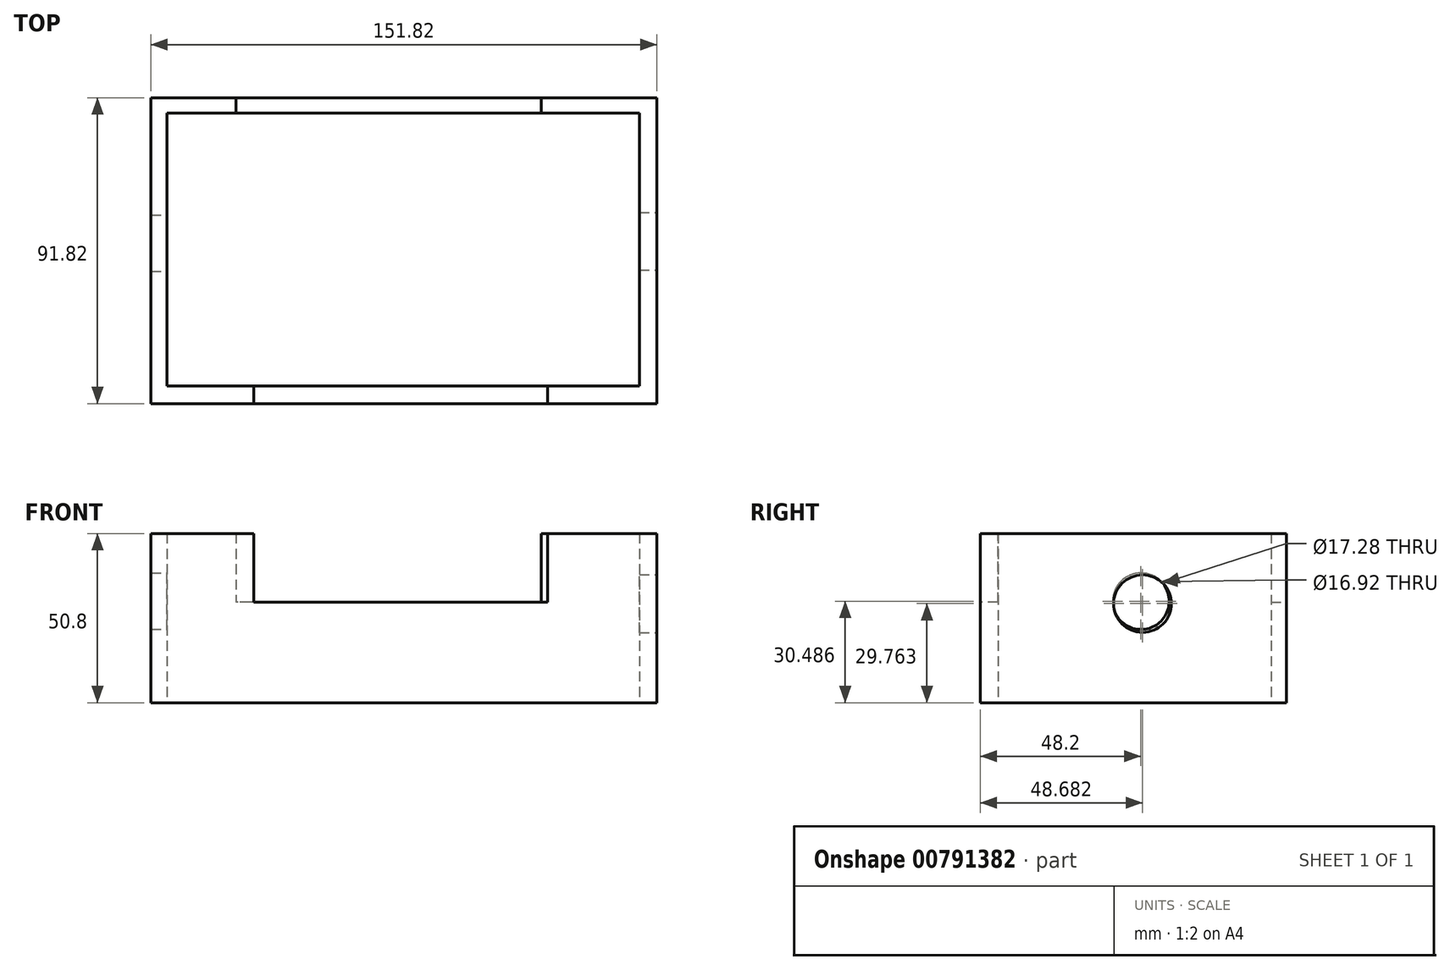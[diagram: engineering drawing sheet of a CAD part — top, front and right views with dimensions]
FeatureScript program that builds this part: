
annotation { "Feature Type Name" : "Feature", "Feature Type Description" : "" }
export const myFeature = defineFeature(function(context is Context, id is Id, definition is map)
    precondition{}
    {
        {
            var Q0;
            Q0=qCreatedBy(makeId("Top.planeOp"),FACE);
            var sketch = newSketch(context, id + "F0", { "sketchPlane" : qUnion([Q0])});
            skLineSegment(sketch, "E0.bottom", {"start": v(-76.03, 36.27) * mm, "end": v(75.8, 36.27) * mm});
            skLineSegment(sketch, "E0.top", {"start": v(-76.03, -55.55) * mm, "end": v(75.8, -55.55) * mm});
            skLineSegment(sketch, "E0.left", {"start": v(-76.03, 36.27) * mm, "end": v(-76.03, -55.55) * mm});
            skLineSegment(sketch, "E0.right", {"start": v(75.8, 36.27) * mm, "end": v(75.8, -55.55) * mm});
            skLineSegment(sketch, "E1.bottom", {"start": v(-71.21, 31.7) * mm, "end": v(70.5, 31.7) * mm});
            skLineSegment(sketch, "E1.top", {"start": v(-71.21, -50.25) * mm, "end": v(70.5, -50.25) * mm});
            skLineSegment(sketch, "E1.left", {"start": v(-71.21, 31.7) * mm, "end": v(-71.21, -50.25) * mm});
            skLineSegment(sketch, "E1.right", {"start": v(70.5, 31.7) * mm, "end": v(70.5, -50.25) * mm});
            skSolve(sketch);
        }
        {
            var Q0;
            Q0=makeQuery(id+"F0.imprint","IMPRINT",FACE,{"disambiguationData":[TD([[makeQuery(id+"F0.imprint","IMPRINT",EDGE,{"derivedFrom":sQuery(id+"F0.wireOp",EDGE,"E0.bottom")}),-1.0]])]});
            extrude(context, id + "F1", {"entities" : qUnion([Q0]), "depth" : 50.8 * mm, "offsetDistance" : 25.4 * mm});
        }
        {
            var Q0;
            Q0=makeQuery(id+"F1.opExtrude","SWEPT_FACE",FACE,{"disambiguationData":[OSD([sQuery(id+"F0.wireOp",EDGE,"E0.top")])]});
            var sketch = newSketch(context, id + "F2", { "sketchPlane" : qUnion([Q0])});
            skLineSegment(sketch, "E2.bottom", {"start": v(-45.2, 50.8) * mm, "end": v(42.95, 50.8) * mm});
            skLineSegment(sketch, "E2.top", {"start": v(-45.2, 30.18) * mm, "end": v(42.95, 30.18) * mm});
            skLineSegment(sketch, "E2.left", {"start": v(-45.2, 50.8) * mm, "end": v(-45.2, 30.18) * mm});
            skLineSegment(sketch, "E2.right", {"start": v(42.95, 50.8) * mm, "end": v(42.95, 30.18) * mm});
            skSolve(sketch);
        }
        {
            var Q0;
            Q0=makeQuery(id+"F2.imprint","IMPRINT",FACE,{"disambiguationData":[TD([[makeQuery(id+"F2.imprint","IMPRINT",EDGE,{"derivedFrom":sQuery(id+"F2.wireOp",EDGE,"E2.bottom")}),-1.0]])]});
            extrude(context, id + "F3", {"entities" : qUnion([Q0]), "operationType" : NewBodyOperationType.REMOVE, "oppositeDirection" : true, "depth" : 25.4 * mm, "offsetDistance" : 25.4 * mm});
        }
        {
            var Q0;
            Q0=makeQuery(id+"F1.opExtrude","SWEPT_FACE",FACE,{"disambiguationData":[OSD([sQuery(id+"F0.wireOp",EDGE,"E0.right")])]});
            var sketch = newSketch(context, id + "F4", { "sketchPlane" : qUnion([Q0])});
            skCircle(sketch, "E3", {"center": v(-6.87, 29.76) * mm, "radius": 8.64 * mm});
            skSolve(sketch);
        }
        {
            var Q0;
            Q0=makeQuery(id+"F4.imprint","IMPRINT",FACE,{"disambiguationData":[TD([[makeQuery(id+"F4.imprint","IMPRINT",EDGE,{"derivedFrom":sQuery(id+"F4.wireOp",EDGE,"E3")}),1.0]])]});
            extrude(context, id + "F5", {"entities" : qUnion([Q0]), "operationType" : NewBodyOperationType.REMOVE, "oppositeDirection" : true, "depth" : 25.4 * mm, "offsetDistance" : 25.4 * mm});
        }
        {
            var Q0;
            Q0=makeQuery(id+"F1.opExtrude","SWEPT_FACE",FACE,{"disambiguationData":[OSD([sQuery(id+"F0.wireOp",EDGE,"E1.left")])]});
            var sketch = newSketch(context, id + "F6", { "sketchPlane" : qUnion([Q0])});
            skCircle(sketch, "E4", {"center": v(-7.35, 30.49) * mm, "radius": 8.46 * mm});
            skSolve(sketch);
        }
        {
            var Q0;
            Q0 = qSketchRegion(id + "F6", true);
            extrude(context, id + "F7", {"entities" : qUnion([Q0]), "operationType" : NewBodyOperationType.REMOVE, "oppositeDirection" : true, "depth" : 25.4 * mm, "offsetDistance" : 25.4 * mm});
        }
        {
            var Q0;
            Q0=makeQuery(id+"F1.opExtrude","SWEPT_FACE",FACE,{"disambiguationData":[OSD([sQuery(id+"F0.wireOp",EDGE,"E0.bottom")])]});
            var sketch = newSketch(context, id + "F8", { "sketchPlane" : qUnion([Q0])});
            skLineSegment(sketch, "E5.bottom", {"start": v(-41.09, 50.8) * mm, "end": v(50.49, 50.8) * mm});
            skLineSegment(sketch, "E5.top", {"start": v(-41.09, 30.25) * mm, "end": v(50.49, 30.25) * mm});
            skLineSegment(sketch, "E5.left", {"start": v(-41.09, 50.8) * mm, "end": v(-41.09, 30.25) * mm});
            skLineSegment(sketch, "E5.right", {"start": v(50.49, 50.8) * mm, "end": v(50.49, 30.25) * mm});
            skSolve(sketch);
        }
        {
            var Q0;
            Q0 = qSketchRegion(id + "F8", true);
            extrude(context, id + "F9", {"entities" : qUnion([Q0]), "operationType" : NewBodyOperationType.REMOVE, "oppositeDirection" : true, "depth" : 25.4 * mm, "offsetDistance" : 25.4 * mm});
        }
    });
